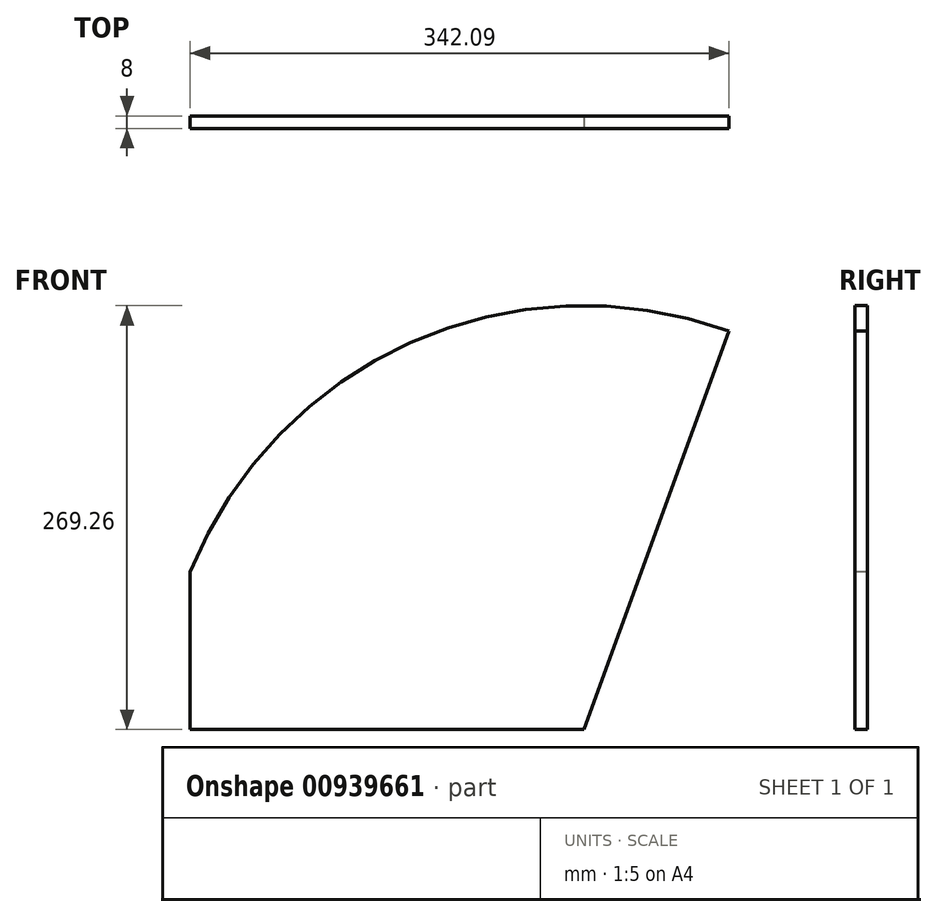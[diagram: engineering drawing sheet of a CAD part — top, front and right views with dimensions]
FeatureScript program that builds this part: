
annotation { "Feature Type Name" : "Feature", "Feature Type Description" : "" }
export const myFeature = defineFeature(function(context is Context, id is Id, definition is map)
    precondition{}
    {
        {
            var Q0;
            Q0=qCreatedBy(makeId("Front.planeOp"),FACE);
            var sketch = newSketch(context, id + "F0", { "sketchPlane" : qUnion([Q0])});
            skLineSegment(sketch, "E0", {"start": v(0, 0) * mm, "end": v(250, 0) * mm});
            skLineSegment(sketch, "E1", {"start": v(0, 0) * mm, "end": v(0, 100) * mm});
            skLineSegment(sketch, "E2", {"start": v(250, 0) * mm, "end": v(342.1, 253.02) * mm});
            skArc(sketch, "E3", {"start": v(0, 100) * mm, "mid": v(140.06, 245.79) * mm, "end": v(342.1, 253.02) * mm});
            skSolve(sketch);
        }
        {
            var Q0;
            Q0 = qSketchRegion(id + "F0", true);
            extrude(context, id + "F1", {"entities" : qUnion([Q0]), "oppositeDirection" : true, "depth" : 8 * mm, "offsetDistance" : 25 * mm});
        }
    });
